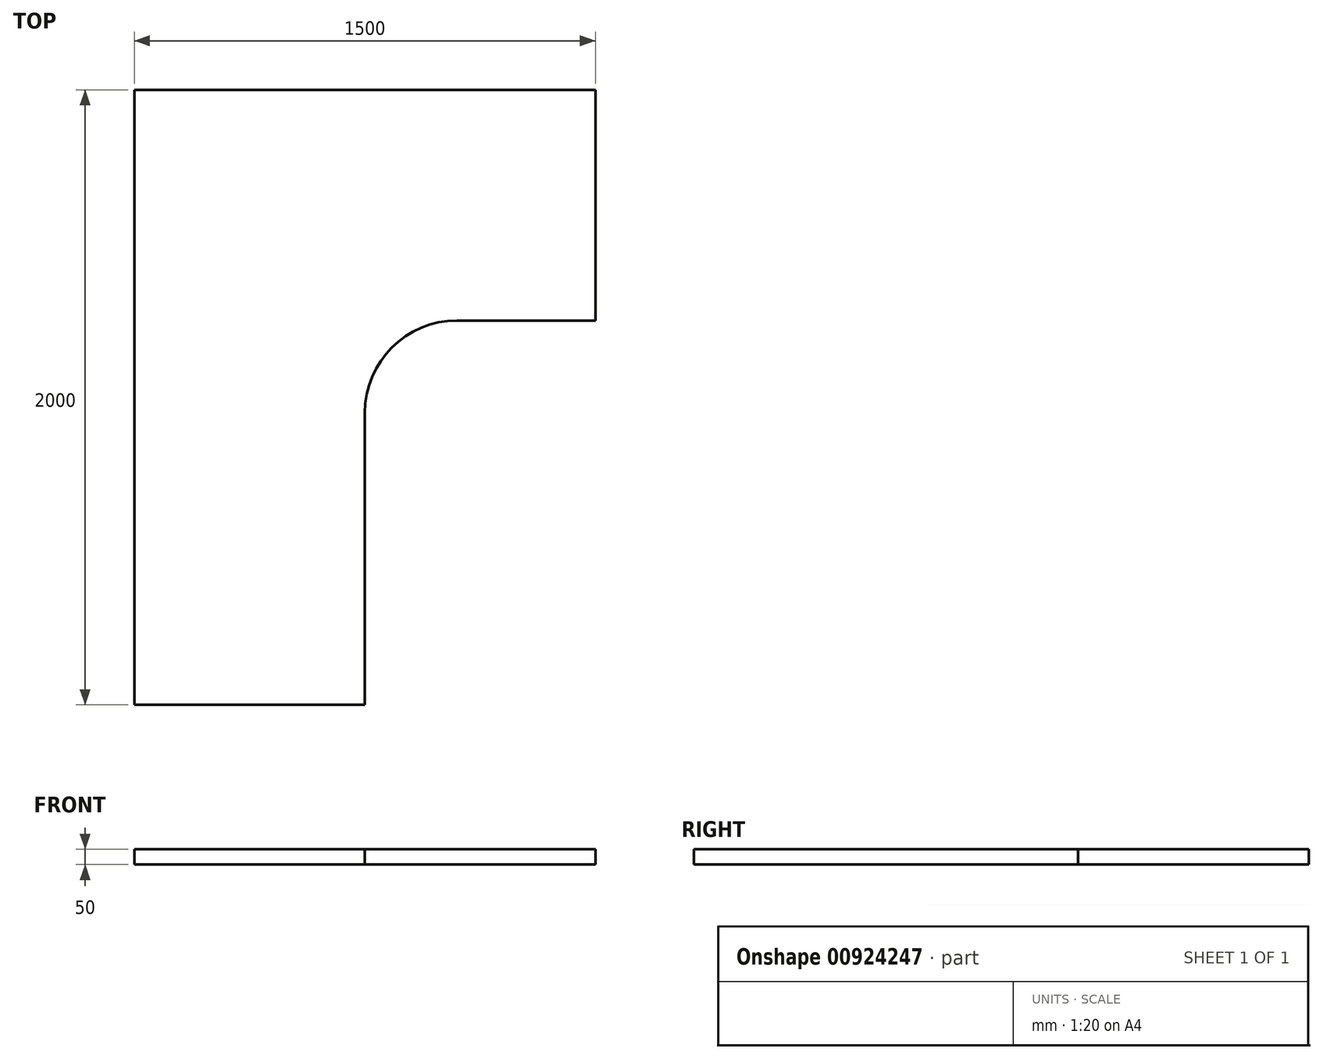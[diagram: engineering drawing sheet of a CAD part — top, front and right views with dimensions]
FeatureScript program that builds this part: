
annotation { "Feature Type Name" : "Feature", "Feature Type Description" : "" }
export const myFeature = defineFeature(function(context is Context, id is Id, definition is map)
    precondition{}
    {
        {
            var Q0;
            Q0=qCreatedBy(makeId("Top.planeOp"),FACE);
            var sketch = newSketch(context, id + "F0", { "sketchPlane" : qUnion([Q0]), "disableImprinting" : false});
            skLineSegment(sketch, "E0.bottom", {"start": v(-750, 750) * mm, "end": v(750, 750) * mm});
            skLineSegment(sketch, "E0.top", {"start": v(-750, -1250) * mm, "end": v(750, -1250) * mm});
            skLineSegment(sketch, "E0.left", {"start": v(-750, 750) * mm, "end": v(-750, -1250) * mm});
            skLineSegment(sketch, "E0.right", {"start": v(750, 750) * mm, "end": v(750, -1250) * mm});
            skSolve(sketch);
        }
        {
            assignVariable(context, id + "F1", {"name" : "d", "anyValue" : 750});
        }
        {
            var Q0;
            Q0=qCreatedBy(makeId("Top.planeOp"),FACE);
            cPlane(context, id + "F2", {"entities" : qUnion([Q0]), "cplaneType" : CPlaneType.OFFSET, "offset" : (getVariable(context, 'd')) * mm, "width" : 150 * mm, "height" : 150 * mm});
        }
        {
            var Q0;
            Q0=qCreatedBy(id+"F2.planeOp",FACE);
            var sketch = newSketch(context, id + "F3", { "sketchPlane" : qUnion([Q0])});
            skPoint(sketch, "E1.0", {"position": v(750, 750) * mm});
            skPoint(sketch, "E2.0", {"position": v(-750, 750) * mm});
            skPoint(sketch, "E3.0", {"position": v(-750, -1250) * mm});
            skLineSegment(sketch, "E4", {"start": v(300, 0) * mm, "end": v(750, 0) * mm});
            skLineSegment(sketch, "E5", {"start": v(750, 0) * mm, "end": v(750, 750) * mm});
            skLineSegment(sketch, "E6", {"start": v(-750, 750) * mm, "end": v(-750, -1250) * mm});
            skLineSegment(sketch, "E7", {"start": v(0, -1250) * mm, "end": v(0, -300) * mm});
            skLineSegment(sketch, "E8", {"start": v(-750, 750) * mm, "end": v(750, 750) * mm});
            skLineSegment(sketch, "E9", {"start": v(-750, -1250) * mm, "end": v(0, -1250) * mm});
            skPoint(sketch, "E10.visualSharp", {"position": v(0, 0) * mm});
            skArc(sketch, "E10.filletArc", {"start": v(300, 0) * mm, "mid": v(87.87, -87.87) * mm, "end": v(0, -300) * mm});
            skSolve(sketch);
        }
        {
            assignVariable(context, id + "F4", {"name" : "h", "anyValue" : 1000});
        }
        {
            var Q0;
            Q0=qCreatedBy(id+"F2.planeOp",FACE);
            cPlane(context, id + "F5", {"entities" : qUnion([Q0]), "cplaneType" : CPlaneType.OFFSET, "offset" : (getVariable(context, 'h')) * mm, "width" : 150 * mm, "height" : 150 * mm});
        }
        {
            var Q0;
            Q0=qCreatedBy(id+"F5.planeOp",FACE);
            var sketch = newSketch(context, id + "F6", { "sketchPlane" : qUnion([Q0])});
            skPoint(sketch, "E11", {"position": v(-250, -350) * mm});
            skPoint(sketch, "E12", {"position": v(350, 250) * mm});
            skPoint(sketch, "E13.0", {"position": v(300, -300) * mm});
            skArc(sketch, "E14.0", {"start": v(300, 250) * mm, "mid": v(-88.9, 88.9) * mm, "end": v(-250, -300) * mm, "construction": true});
            skPoint(sketch, "E15.0", {"position": v(-750, 750) * mm});
            skLineSegment(sketch, "E16", {"start": v(-750, 750) * mm, "end": v(300, -300) * mm, "construction": true});
            skPoint(sketch, "E17", {"position": v(-88.9, 88.9) * mm});
            skPoint(sketch, "E18", {"position": v(700, 250) * mm});
            skSolve(sketch);
        }
        {
            var Q0;
            Q0=qCreatedBy(makeId("Top.planeOp"),FACE);
            var sketch = newSketch(context, id + "F7", { "sketchPlane" : qUnion([Q0])});
            skPoint(sketch, "E19.0", {"position": v(-88.9, 88.9) * mm});
            skCircle(sketch, "E20", {"center": v(-88.9, 88.9) * mm, "radius": 568.6 * mm});
            skPoint(sketch, "E21.0", {"position": v(350, 250) * mm});
            skPoint(sketch, "E22.0", {"position": v(-250, -350) * mm});
            skCircle(sketch, "E23", {"center": v(350, 250) * mm, "radius": 568.6 * mm});
            skCircle(sketch, "E24", {"center": v(-250, -350) * mm, "radius": 568.6 * mm});
            skPoint(sketch, "E25.0", {"position": v(700, 250) * mm});
            skCircle(sketch, "E26", {"center": v(700, 250) * mm, "radius": 568.6 * mm});
            skSolve(sketch);
        }
        {
            var Q0;
            Q0=makeQuery(id+"F7.imprint","IMPRINT",FACE,{"disambiguationData":[TD([[makeQuery(id+"F7.imprint","IMPRINT",EDGE,{"derivedFrom":sQuery(id+"F7.wireOp",EDGE,"E20")}),1.0]])]});
            var Q1;
            Q1=sQuery(id+"F6.wireOp",VERTEX,"cbbe6bf4-1df4-4786-b697-ca3d39312b80");
            var Q2;
            Q2=sQuery(id+"F7.wireOp",EDGE,"E20");
            var Q3;
            Q3=sQuery(id+"F6.wireOp",VERTEX,"E17");
            loft(context, id + "F8", {"bodyType" : ToolBodyType.SURFACE, "sheetProfilesArray" : [{ "sheetProfileEntities" : qUnion([Q0]) }, { "sheetProfileEntities" : qUnion([Q1]) }], "wireProfilesArray" : [{ "wireProfileEntities" : qUnion([Q2]) }, { "wireProfileEntities" : qUnion([Q3]) }]});
        }
        {
            var Q0;
            Q0=makeQuery(id+"F3.imprint","IMPRINT",FACE,{"disambiguationData":[TD([[makeQuery(id+"F3.imprint","IMPRINT",EDGE,{"derivedFrom":sQuery(id+"F3.wireOp",EDGE,"E4")}),1.0]])]});
            extrude(context, id + "F9", {"entities" : qUnion([Q0]), "oppositeDirection" : true, "depth" : 50 * mm, "offsetDistance" : 25 * mm});
        }
        {
            var Q1;
            {var subQ0=sQuery(id+"F7.wireOp",EDGE,"E23");var subQ1=sQuery(id+"F7.wireOp",EDGE,"E20");var subQ2=makeQuery(id+"F7.imprint","INTERSECT",VERTEX,{"disambiguationData":[OD(0.0)],"derivedFrom":[subQ1,subQ0]});Q1=makeQuery(id+"F7.imprint","IMPRINT",FACE,{"disambiguationData":[TD([[makeQuery(id+"F7.imprint","IMPRINT",EDGE,{"disambiguationData":[TD([[subQ2,1.0]])],"derivedFrom":subQ1}),-1.0]])]});}
            var Q2;
            {var subQ0=sQuery(id+"F7.wireOp",EDGE,"E23");var subQ1=sQuery(id+"F7.wireOp",EDGE,"E20");var subQ2=makeQuery(id+"F7.imprint","INTERSECT",VERTEX,{"disambiguationData":[OD(1.0)],"derivedFrom":[subQ1,subQ0]});Q2=makeQuery(id+"F7.imprint","IMPRINT",FACE,{"disambiguationData":[TD([[makeQuery(id+"F7.imprint","IMPRINT",EDGE,{"disambiguationData":[TD([[subQ2,-1.0]])],"derivedFrom":subQ1}),1.0]])]});}
            var Q3;
            {var subQ0=sQuery(id+"F7.wireOp",EDGE,"E23");var subQ1=sQuery(id+"F7.wireOp",EDGE,"E20");var subQ2=makeQuery(id+"F7.imprint","INTERSECT",VERTEX,{"disambiguationData":[OD(0.0)],"derivedFrom":[subQ1,subQ0]});Q3=makeQuery(id+"F7.imprint","IMPRINT",FACE,{"disambiguationData":[TD([[makeQuery(id+"F7.imprint","IMPRINT",EDGE,{"disambiguationData":[TD([[subQ2,1.0]])],"derivedFrom":subQ1}),1.0]])]});}
            var Q4;
            Q4=sQuery(id+"F6.wireOp",VERTEX,"E12");
            var Q5;
            Q5=sQuery(id+"F7.wireOp",EDGE,"E23");
            var Q6;
            Q6=sQuery(id+"F6.wireOp",VERTEX,"E12");
            loft(context, id + "F10", {"bodyType" : ToolBodyType.SURFACE, "sheetProfilesArray" : [{ "sheetProfileEntities" : qUnion([Q1]) }, { "sheetProfileEntities" : qUnion([Q2]) }, { "sheetProfileEntities" : qUnion([Q3]) }, { "sheetProfileEntities" : qUnion([Q4]) }], "wireProfilesArray" : [{ "wireProfileEntities" : qUnion([Q5]) }, { "wireProfileEntities" : qUnion([Q6]) }]});
        }
        {
            var Q0;
            Q0=sQuery(id+"F7.wireOp",EDGE,"E24");
            var Q1;
            Q1=sQuery(id+"F6.wireOp",VERTEX,"E11");
            loft(context, id + "F11", {"bodyType" : ToolBodyType.SURFACE, "wireProfilesArray" : [{ "wireProfileEntities" : qUnion([Q0]) }, { "wireProfileEntities" : qUnion([Q1]) }]});
        }
        {
            var Q0;
            Q0=sQuery(id+"F7.wireOp",EDGE,"E26");
            var Q1;
            Q1=sQuery(id+"F6.wireOp",VERTEX,"E18");
            loft(context, id + "F12", {"bodyType" : ToolBodyType.SURFACE, "wireProfilesArray" : [{ "wireProfileEntities" : qUnion([Q0]) }, { "wireProfileEntities" : qUnion([Q1]) }]});
        }
    });
